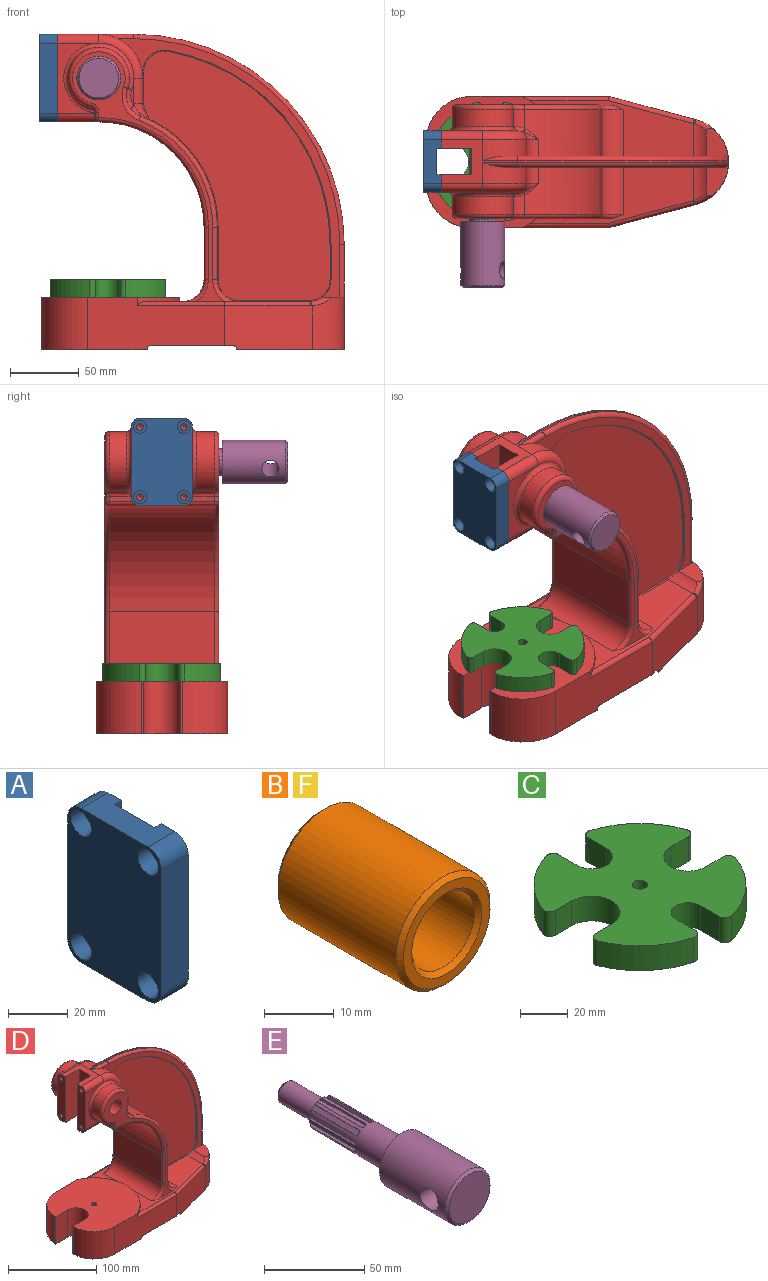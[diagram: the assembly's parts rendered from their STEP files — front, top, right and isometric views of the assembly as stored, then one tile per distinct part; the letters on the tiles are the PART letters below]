
ASSEMBLY  parts=6 mates=4
PART A: 26 faces, bbox 12.7x44.5x63.5 mm
  f0: plane 63.5x12.7mm, normal (1,0,0), area 753.5mm2, adj f1,f2,f6,f7,f8,f14,f17,f25
  f1: cylinder r=6.35mm len=12.7mm, axis (1,0,0), area 126.7mm2, adj f0,f2,f8,f9
  f2: plane 31.75x12.7mm, normal (0,0,1), area 341.8mm2, adj f0,f1,f3,f9,f10,f23,f24,f25
  f3: cylinder r=6.35mm len=12.7mm, axis (1,0,0), area 126.7mm2, adj f2,f4,f9,f10
  f4: plane 50.8x12.7mm, normal (0,1,0), area 645.2mm2, adj f3,f5,f9,f10
  f5: cylinder r=6.35mm len=12.7mm, axis (1,0,0), area 126.7mm2, adj f4,f6,f9,f10
  f6: plane 31.75x12.7mm, normal (0,0,-1), area 341.8mm2, adj f0,f5,f7,f9,f10,f23,f24,f25
  f7: cylinder r=6.35mm len=12.7mm, axis (1,0,0), area 126.7mm2, adj f0,f6,f8,f9
  f8: plane 50.8x12.7mm, normal (0,-1,0), area 645.2mm2, adj f0,f1,f7,f9
  f9: plane 63.5x44.45mm, normal (-1,0,0), area 2502.9mm2, adj f1,f2,f3,f4,f5,f6,f7,f8
  f10: plane 63.5x12.7mm, normal (1,0,0), area 753.5mm2, adj f2,f3,f4,f5,f6,f11,f20,f24
  f11: cylinder r=2.38mm len=6.35mm, axis (-1,0,0), area 95mm2, adj f10,f12
  f12: plane 9.53x9.53mm, normal (-1,0,0), area 53.4mm2, adj f11,f13
  f13: cylinder r=4.76mm len=9.53mm, axis (-1,0,0), area 190mm2, adj f9,f12
  f14: cylinder r=2.38mm len=6.35mm, axis (-1,0,0), area 95mm2, adj f0,f15
  f15: plane 9.53x9.53mm, normal (-1,0,0), area 53.4mm2, adj f14,f16
  f16: cylinder r=4.76mm len=9.53mm, axis (-1,0,0), area 190mm2, adj f9,f15
  f17: cylinder r=2.38mm len=6.35mm, axis (-1,0,0), area 95mm2, adj f0,f18
  f18: plane 9.53x9.53mm, normal (-1,0,0), area 53.4mm2, adj f17,f19
  f19: cylinder r=4.76mm len=9.53mm, axis (-1,0,0), area 190mm2, adj f9,f18
  f20: cylinder r=2.38mm len=6.35mm, axis (-1,0,0), area 95mm2, adj f10,f21
  f21: plane 9.53x9.53mm, normal (-1,0,0), area 53.4mm2, adj f20,f22
  f22: cylinder r=4.76mm len=9.53mm, axis (-1,0,0), area 190mm2, adj f9,f21
  f23: plane 63.5x19.05mm, normal (1,0,0), area 1209.7mm2, adj f2,f6,f24,f25
  f24: plane 63.5x3.23mm, normal (0,-1,0), area 204.8mm2, adj f2,f6,f10,f23
  f25: plane 63.5x3.23mm, normal (0,1,0), area 204.8mm2, adj f0,f2,f6,f23
PART B: 8 faces, bbox 19.1x25.4x19.1 mm
  f0: plane 17.53x17.53mm, normal (0,-1,0), area 82.3mm2, adj f4,f5
  f1: plane 17.53x17.53mm, normal (0,1,0), area 82.3mm2, adj f6,f7
  f2: cylinder r=9.53mm len=23.88mm, axis (0,1,0), area 1428.9mm2, adj f4,f7
  f3: cylinder r=6.35mm len=23.88mm, axis (0,1,0), area 952.6mm2, adj f5,f6
  f4: cone r=9.53mm half-angle=45deg, axis (0,1,0), area 61.9mm2, adj f0,f2
  f5: cone r=6.35mm half-angle=45deg, axis (0,-1,0), area 45.6mm2, adj f0,f3
  f6: cone r=6.35mm half-angle=45deg, axis (0,1,0), area 45.6mm2, adj f1,f3
  f7: cone r=9.53mm half-angle=45deg, axis (0,-1,0), area 61.9mm2, adj f1,f2
PART C: 27 faces, bbox 83.8x85.8x12.7 mm
  f0: cylinder r=44.45mm len=28.56mm, axis (0,0,-1), area 510.6mm2, adj f17,f18,f19,f25
  f1: plane 12.7x9.85mm, normal (0,-1,0), area 125.1mm2, adj f2,f17,f18,f25
  f2: cylinder r=11.9mm len=23.8mm, axis (0,0,-1), area 474.8mm2, adj f1,f3,f17,f18
  f3: plane 12.7x9.85mm, normal (0,1,0), area 125.1mm2, adj f2,f17,f18,f26
  f4: cylinder r=44.45mm len=30.27mm, axis (0,0,-1), area 533.1mm2, adj f17,f18,f20,f26
  f5: plane 12.7x11.39mm, normal (1,0,0), area 144.7mm2, adj f6,f17,f18,f20
  f6: cylinder r=7.14mm len=14.28mm, axis (0,0,-1), area 284.8mm2, adj f5,f7,f17,f18
  f7: plane 12.7x11.39mm, normal (-1,0,0), area 144.7mm2, adj f6,f17,f18,f21
  f8: cylinder r=44.45mm len=30.9mm, axis (0,0,-1), area 556.3mm2, adj f17,f18,f21,f22
  f9: plane 12.7x10.43mm, normal (0,1,0), area 132.5mm2, adj f10,f17,f18,f22
  f10: cylinder r=10.31mm len=20.62mm, axis (0,0,-1), area 411.4mm2, adj f9,f11,f17,f18
  f11: plane 12.7x10.43mm, normal (0,-1,0), area 132.5mm2, adj f10,f17,f18,f23
  f12: cylinder r=44.45mm len=29.19mm, axis (0,0,-1), area 533.7mm2, adj f17,f18,f23,f24
  f13: plane 12.7x10.95mm, normal (-1,0,0), area 139mm2, adj f14,f17,f18,f24
  f14: cylinder r=8.72mm len=17.45mm, axis (0,0,-1), area 348.1mm2, adj f13,f15,f17,f18
  f15: plane 12.7x10.95mm, normal (1,0,0), area 139mm2, adj f14,f17,f18,f19
  f16: cylinder r=3.17mm len=12.7mm, axis (0,0,-1), area 253.4mm2, adj f17,f18
  f17: plane 85.84x83.78mm, normal (0,0,1), area 4373.8mm2, adj f0,f1,f2,f3,f4,f5,f6,f7
  f18: plane 85.84x83.78mm, normal (0,0,-1), area 4373.8mm2, adj f0,f1,f2,f3,f4,f5,f6,f7
  f19: cylinder r=3.17mm len=12.7mm, axis (0,0,-1), area 75.1mm2, adj f0,f15,f17,f18
  f20: cylinder r=3.17mm len=12.7mm, axis (0,0,-1), area 73.5mm2, adj f4,f5,f17,f18
  f21: cylinder r=3.17mm len=12.7mm, axis (0,0,-1), area 73.5mm2, adj f7,f8,f17,f18
  f22: cylinder r=3.17mm len=12.7mm, axis (0,0,-1), area 76.8mm2, adj f8,f9,f17,f18
  f23: cylinder r=3.17mm len=12.7mm, axis (0,0,-1), area 76.8mm2, adj f11,f12,f17,f18
  f24: cylinder r=3.17mm len=12.7mm, axis (0,0,-1), area 75.1mm2, adj f12,f13,f17,f18
  f25: cylinder r=3.17mm len=12.7mm, axis (0,0,-1), area 78.4mm2, adj f0,f1,f17,f18
  f26: cylinder r=3.17mm len=12.7mm, axis (0,0,-1), area 78.4mm2, adj f3,f4,f17,f18
PART D: 180 faces, bbox 234.5x98.1x244 mm
  f0: plane 63.5x12.7mm, normal (-1,0,0), area 753.5mm2, adj f2,f15,f17,f92,f97,f149,f151,f158
  f1: plane 20.23x2.34mm, normal (0,1,0), area 23.9mm2, adj f90,f91,f104,f106
  f2: plane 50.8x30.1mm, normal (0,-1,0), area 515.4mm2, adj f0,f83,f92,f97,f124
  f3: plane 22.59x12.73mm, normal (1,0,0), area 235.4mm2, adj f19,f26,f32,f87,f94,f174
  f4: plane 22.59x12.73mm, normal (1,0,0), area 235.4mm2, adj f10,f14,f33,f86,f90,f164
  f5: plane 99.19x38.1mm, normal (0,-1,0), area 3202mm2, adj f6,f40,f46,f49,f52,f58,f76,f133
  f6: plane 100x95.25mm, normal (0,0,1), area 7398mm2, adj f5,f43,f44,f48,f54,f55,f56,f57
  f7: plane 38.1x34.96mm, normal (1,0,0), area 1331.9mm2, adj f8,f9,f114,f169
  f8: cylinder r=15.88mm len=34.96mm, axis (0,1,0), area 871.7mm2, adj f7,f37,f115,f167
  f9: cylinder r=85.72mm len=80.21mm, axis (0,1,0), area 3442.3mm2, adj f7,f80,f86,f100,f113,f168
  f10: cylinder r=15.88mm len=18.65mm, axis (0,1,0), area 22.7mm2, adj f4,f11,f33,f162
  f11: cylinder r=142.88mm len=140.67mm, axis (0,1,0), area 163.3mm2, adj f10,f12,f33,f160
  f12: plane 25.4x0.82mm, normal (-1,0,0), area 20.8mm2, adj f11,f13,f33,f161
  f13: cylinder r=15.88mm len=24.81mm, axis (0,1,0), area 242.1mm2, adj f12,f33,f37,f45,f139,f140,f163
  f14: cylinder r=31.75mm len=31.75mm, axis (0,1,0), area 616.8mm2, adj f4,f15,f33,f89,f141
  f15: plane 55.5x31.75mm, normal (0,0,1), area 573.2mm2, adj f0,f14,f16,f19,f31,f88,f92,f141
  f16: plane 63.5x12.7mm, normal (-1,0,0), area 753.5mm2, adj f15,f17,f21,f88,f96,f147,f153,f157
  f17: plane 31.75x30.1mm, normal (0,0,-1), area 533.2mm2, adj f0,f16,f18,f96,f97,f156,f157,f158
  f18: cylinder r=76.2mm len=76.2mm, axis (0,1,0), area 9120.7mm2, adj f17,f22,f103,f105,f119,f121
  f19: cylinder r=31.75mm len=31.75mm, axis (0,1,0), area 616.8mm2, adj f3,f15,f32,f93,f144
  f20: plane 20.23x2.34mm, normal (0,-1,0), area 23.9mm2, adj f94,f95,f122,f124
  f21: plane 50.8x30.1mm, normal (0,1,0), area 515.4mm2, adj f16,f78,f88,f96,f106
  f22: plane 76.2x38.1mm, normal (-1,0,0), area 2903.2mm2, adj f18,f98,f101,f117
  f23: cylinder r=15.88mm len=34.96mm, axis (0,1,0), area 871.7mm2, adj f24,f37,f132,f177
  f24: plane 38.1x34.96mm, normal (1,0,0), area 1331.9mm2, adj f23,f25,f131,f179
  f25: cylinder r=85.72mm len=80.21mm, axis (0,1,0), area 3442.3mm2, adj f24,f81,f87,f118,f130,f178
  f26: cylinder r=15.88mm len=18.65mm, axis (0,1,0), area 22.7mm2, adj f3,f27,f32,f172
  f27: cylinder r=142.88mm len=140.67mm, axis (0,1,0), area 163.3mm2, adj f26,f28,f32,f170
  f28: plane 25.4x0.82mm, normal (-1,0,0), area 20.8mm2, adj f27,f29,f32,f171
  f29: cylinder r=15.88mm len=24.81mm, axis (0,1,0), area 242.1mm2, adj f28,f32,f36,f37,f135,f136,f173
  f30: plane 76.2x7.92mm, normal (1,0,0), area 361.9mm2, adj f31,f36,f42,f45,f51,f53,f143,f146
  f31: cylinder r=152.4mm len=152.4mm, axis (0,1,0), area 377mm2, adj f15,f30,f142,f145
  f32: plane 187.33x160.79mm, normal (0,-1,0), area 1900.4mm2, adj f3,f19,f26,f27,f28,f29,f36,f144
  f33: plane 187.33x160.79mm, normal (0,1,0), area 1900.4mm2, adj f4,f10,f11,f12,f13,f14,f45,f141
  f34: plane 180.67x135mm, normal (0,-1,0), area 14138.8mm2, adj f170,f171,f172,f173,f174,f175,f176,f177
  f35: plane 180.67x135mm, normal (0,1,0), area 14138.8mm2, adj f160,f161,f162,f163,f164,f165,f166,f167
  f36: plane 26.58x18.73mm, normal (0,0,1), area 245.8mm2, adj f29,f30,f32,f53,f136,f146
  f37: plane 119.12x89.67mm, normal (0,0,1), area 4280.2mm2, adj f8,f13,f23,f29,f76,f77,f84,f98
  f38: cylinder r=3.17mm len=9.06mm, axis (0,1,0), area 40.9mm2, adj f40,f42,f52,f69
  f39: cylinder r=3.17mm len=7.93mm, axis (0,1,0), area 39.5mm2, adj f41,f46,f48,f65
  f40: plane 58.73x9.7mm, normal (0,0,-1), area 467.1mm2, adj f5,f38,f49,f52,f64,f69
  f41: plane 58.73x9.7mm, normal (0,0,-1), area 467.1mm2, adj f39,f47,f48,f50,f65,f67
  f42: plane 90.55x77.8mm, normal (0,0,-1), area 1454mm2, adj f30,f38,f47,f50,f51,f52,f53,f59
  f43: plane 38.1x1.61mm, normal (-1,0,0), area 61.5mm2, adj f6,f46,f54,f58
  f44: plane 38.1x1.61mm, normal (-1,0,0), area 61.5mm2, adj f6,f46,f55,f57
  f45: plane 26.58x18.73mm, normal (0,0,1), area 245.8mm2, adj f13,f30,f33,f51,f140,f143
  f46: plane 95.25x76.2mm, normal (0,0,-1), area 2029.8mm2, adj f5,f39,f43,f44,f48,f49,f54,f55
  f47: cylinder r=3.17mm len=9.06mm, axis (0,1,0), area 40.9mm2, adj f41,f42,f50,f67
  f48: plane 99.19x38.1mm, normal (0,1,0), area 3202mm2, adj f6,f39,f41,f46,f50,f57,f76,f137
  f49: cylinder r=3.17mm len=7.93mm, axis (0,1,0), area 39.5mm2, adj f5,f40,f46,f64
  f50: plane 63.64x32.15mm, normal (0.26,0.97,0), area 2053.6mm2, adj f41,f42,f47,f48,f51,f138,f139
  f51: cylinder r=31.75mm len=38.1mm, axis (0,0,-1), area 1379.2mm2, adj f30,f42,f45,f50,f140
  f52: plane 63.64x32.15mm, normal (0.26,-0.97,0), area 2053.6mm2, adj f5,f38,f40,f42,f53,f134,f135
  f53: cylinder r=31.75mm len=38.1mm, axis (0,0,-1), area 1379.2mm2, adj f30,f36,f42,f52,f136
  f54: plane 38.1x19.05mm, normal (0,1,0), area 725.8mm2, adj f6,f43,f46,f56
  f55: plane 38.1x19.05mm, normal (0,-1,0), area 725.8mm2, adj f6,f44,f46,f56
  f56: cylinder r=13.49mm len=38.1mm, axis (0,0,-1), area 1615.1mm2, adj f6,f46,f54,f55
  f57: cylinder r=33.32mm len=38.1mm, axis (0,0,-1), area 1963.7mm2, adj f6,f44,f46,f48
  f58: cylinder r=33.32mm len=38.1mm, axis (0,0,-1), area 1963.7mm2, adj f5,f6,f43,f46
  f59: plane 30.18x6.86mm, normal (-1,0,0), area 207mm2, adj f42,f60,f68,f70
  f60: plane 31.27x5.6mm, normal (0,0,-1), area 124.1mm2, adj f59,f61,f68,f70
  f61: cylinder r=23.8mm len=46.06mm, axis (0,1,0), area 499.2mm2, adj f60,f62,f67,f68,f69,f70
  f62: plane 84.13x79.4mm, normal (0,0,-1), area 5642.5mm2, adj f61,f64,f65,f66,f67,f69
  f63: plane 100.62x79.4mm, normal (0,0,-1), area 6568.5mm2, adj f64,f65,f66,f71,f72,f73,f74,f75
  f64: plane 98.15x30.18mm, normal (0,1,0), area 2718.8mm2, adj f40,f46,f49,f62,f63,f66,f69,f75
  f65: plane 98.15x30.18mm, normal (0,-1,0), area 2718.8mm2, adj f39,f41,f46,f62,f63,f66,f67,f74
  f66: plane 79.4x3.18mm, normal (-1,0,0), area 252.1mm2, adj f62,f63,f64,f65
  f67: plane 62.63x27.36mm, normal (-0.26,-0.97,0), area 1710.8mm2, adj f41,f42,f47,f61,f62,f65,f68
  f68: cylinder r=23.83mm len=30.18mm, axis (0,0,-1), area 814.8mm2, adj f42,f59,f60,f61,f67
  f69: plane 62.63x27.36mm, normal (-0.26,0.97,0), area 1710.8mm2, adj f38,f40,f42,f61,f62,f64,f70
  f70: cylinder r=23.83mm len=30.18mm, axis (0,0,-1), area 814.8mm2, adj f42,f59,f60,f61,f69
  f71: plane 30.18x10.12mm, normal (0,-1,0), area 305.3mm2, adj f46,f63,f73,f75
  f72: plane 30.18x10.12mm, normal (0,1,0), area 305.3mm2, adj f46,f63,f73,f74
  f73: cylinder r=21.42mm len=42.84mm, axis (0,0,-1), area 2030.4mm2, adj f46,f63,f71,f72
  f74: cylinder r=25.4mm len=30.18mm, axis (0,0,-1), area 986.2mm2, adj f46,f63,f65,f72
  f75: cylinder r=25.4mm len=30.18mm, axis (0,0,-1), area 986.2mm2, adj f46,f63,f64,f71
  f76: cylinder r=52.37mm len=95.25mm, axis (0,0,1), area 401mm2, adj f5,f6,f37,f48,f133,f137
  f77: plane 180.98x110.12mm, normal (0,1,0), area 1717.8mm2, adj f37,f85,f99,f101,f103,f109,f110,f111
  f78: plane 16.73x3.98mm, normal (-1,0,0), area 64.1mm2, adj f21,f96,f105,f106,f108,f109
  f79: cylinder r=22.23mm len=44.45mm, axis (0,1,0), area 1356.2mm2, adj f80,f106,f108,f111
  f80: cylinder r=15.88mm len=20.22mm, axis (0,1,0), area 319.4mm2, adj f9,f79,f102,f104,f112
  f81: cylinder r=15.88mm len=20.22mm, axis (0,1,0), area 319.4mm2, adj f25,f82,f120,f122,f129
  f82: cylinder r=22.23mm len=44.45mm, axis (0,1,0), area 1356.2mm2, adj f81,f124,f126,f128
  f83: plane 16.73x3.98mm, normal (-1,0,0), area 64.1mm2, adj f2,f97,f121,f124,f125,f126
  f84: plane 180.98x110.12mm, normal (0,-1,0), area 1717.8mm2, adj f37,f85,f116,f117,f119,f125,f127,f128
  f85: cylinder r=9.53mm len=82.55mm, axis (0,1,0), area 4727mm2, adj f77,f84,f156,f157,f158,f159
  f86: cylinder r=15.88mm len=14.02mm, axis (0,1,0), area 218.9mm2, adj f4,f9,f91,f166
  f87: cylinder r=15.88mm len=14.02mm, axis (0,1,0), area 218.9mm2, adj f3,f25,f95,f176
  f88: cylinder r=6.35mm len=30.1mm, axis (-1,0,0), area 300.2mm2, adj f15,f16,f21,f89
  f89: torus R=25.4mm, axis (0,-1,0), area 461.3mm2, adj f14,f88,f90,f106
  f90: cylinder r=6.35mm len=18.2mm, axis (0,0,1), area 181.6mm2, adj f1,f4,f89,f91
  f91: torus R=22.23mm, axis (0,-1,0), area 98mm2, adj f1,f86,f90,f100,f102
  f92: cylinder r=6.35mm len=30.1mm, axis (1,0,0), area 300.2mm2, adj f0,f2,f15,f93
  f93: torus R=25.4mm, axis (0,-1,0), area 461.3mm2, adj f19,f92,f94,f124
  f94: cylinder r=6.35mm len=18.2mm, axis (0,0,-1), area 181.6mm2, adj f3,f20,f93,f95
  f95: torus R=22.23mm, axis (0,-1,0), area 98mm2, adj f20,f87,f94,f118,f120
  f96: cylinder r=6.35mm len=30.1mm, axis (1,0,0), area 279.1mm2, adj f16,f17,f21,f78,f105
  f97: cylinder r=6.35mm len=30.1mm, axis (-1,0,0), area 279.1mm2, adj f0,f2,f17,f83,f121
  f98: cylinder r=15.88mm len=76.2mm, axis (0,-1,0), area 1900.2mm2, adj f22,f37,f99,f116
  f99: torus R=19.05mm, axis (0,-1,0), area 107.7mm2, adj f37,f77,f98,f101
  f100: bspline ~12.01x8.85mm, area 17.9mm2, adj f9,f91,f102
  f101: cylinder r=3.17mm len=38.1mm, axis (0,0,-1), area 190mm2, adj f22,f77,f99,f103
  f102: bspline ~10.6x9.56mm, area 36.6mm2, adj f80,f91,f100,f104
  f103: torus R=79.38mm, axis (0,-1,0), area 606mm2, adj f18,f77,f101,f107
  f104: torus R=12.7mm, axis (0,-1,0), area 70.6mm2, adj f1,f80,f102,f106
  f105: cylinder r=3.17mm len=22.23mm, axis (0,1,0), area 97.1mm2, adj f18,f78,f96,f107
  f106: torus R=25.4mm, axis (0,-1,0), area 570mm2, adj f1,f21,f78,f79,f89,f104,f108
  f107: sphere r=3.17mm, area 21.6mm2, adj f103,f105,f109
  f108: cylinder r=3.17mm len=15.82mm, axis (0,1,0), area 59.7mm2, adj f78,f79,f106,f110
  f109: cylinder r=3.17mm len=3.98mm, axis (0,0,-1), area 19.9mm2, adj f77,f78,f107,f110
  f110: torus R=6.35mm, axis (0,-1,0), area 28.5mm2, adj f77,f108,f109,f111
  f111: torus R=19.05mm, axis (0,-1,0), area 504.9mm2, adj f77,f79,f110,f112
  f112: torus R=19.05mm, axis (0,-1,0), area 132.1mm2, adj f77,f80,f111,f113
  f113: torus R=82.55mm, axis (0,-1,0), area 510.4mm2, adj f9,f77,f112,f114
  f114: cylinder r=3.17mm len=38.1mm, axis (0,0,1), area 190mm2, adj f7,f77,f113,f115
  f115: torus R=19.05mm, axis (0,-1,0), area 107.7mm2, adj f8,f37,f77,f114
  f116: torus R=19.05mm, axis (0,-1,0), area 107.7mm2, adj f37,f84,f98,f117
  f117: cylinder r=3.17mm len=38.1mm, axis (0,0,1), area 190mm2, adj f22,f84,f116,f119
  f118: bspline ~11.06x8.44mm, area 17.9mm2, adj f25,f95,f120
  f119: torus R=79.38mm, axis (0,-1,0), area 606mm2, adj f18,f84,f117,f123
  f120: bspline ~9.12x8.99mm, area 36.6mm2, adj f81,f95,f118,f122
  f121: cylinder r=3.17mm len=22.23mm, axis (0,1,0), area 97.1mm2, adj f18,f83,f97,f123
  f122: torus R=12.7mm, axis (0,-1,0), area 70.6mm2, adj f20,f81,f120,f124
  f123: sphere r=3.17mm, area 15.8mm2, adj f119,f121,f125
  f124: torus R=25.4mm, axis (0,-1,0), area 570mm2, adj f2,f20,f82,f83,f93,f122,f126
  f125: cylinder r=3.17mm len=3.98mm, axis (0,0,1), area 19.9mm2, adj f83,f84,f123,f127
  f126: cylinder r=3.17mm len=15.82mm, axis (0,1,0), area 59.7mm2, adj f82,f83,f124,f127
  f127: torus R=6.35mm, axis (0,-1,0), area 28.5mm2, adj f84,f125,f126,f128
  f128: torus R=19.05mm, axis (0,-1,0), area 504.9mm2, adj f82,f84,f127,f129
  f129: torus R=19.05mm, axis (0,-1,0), area 132.1mm2, adj f81,f84,f128,f130
  f130: torus R=82.55mm, axis (0,-1,0), area 510.4mm2, adj f25,f84,f129,f131
  f131: cylinder r=3.17mm len=38.1mm, axis (0,0,-1), area 190mm2, adj f24,f84,f130,f132
  f132: torus R=19.05mm, axis (0,-1,0), area 107.7mm2, adj f23,f37,f84,f131
  f133: cylinder r=3.17mm len=63.09mm, axis (1,0,0), area 298.9mm2, adj f5,f37,f76,f134
  f134: cylinder r=3.17mm len=62.81mm, axis (0.97,0.26,0), area 319mm2, adj f37,f52,f133,f135
  f135: bspline ~3.41x3.21mm, area 6mm2, adj f29,f52,f134,f136
  f136: bspline ~18.95x11.92mm, area 79.7mm2, adj f29,f36,f53,f135
  f137: cylinder r=3.17mm len=63.09mm, axis (-1,0,0), area 298.9mm2, adj f37,f48,f76,f138
  f138: cylinder r=3.17mm len=62.81mm, axis (-0.97,0.26,0), area 319mm2, adj f37,f50,f137,f139
  f139: bspline ~6.89x4.84mm, area 6mm2, adj f13,f50,f138,f140
  f140: bspline ~17.46x11.57mm, area 79.7mm2, adj f13,f45,f51,f139
  f141: cylinder r=3.17mm len=25.4mm, axis (-1,0,0), area 92.2mm2, adj f14,f15,f33,f142
  f142: torus R=149.22mm, axis (0,-1,0), area 1184.9mm2, adj f31,f33,f141,f143
  f143: cylinder r=3.17mm len=38.1mm, axis (0,0,1), area 190mm2, adj f30,f33,f45,f142
  f144: cylinder r=3.17mm len=25.4mm, axis (1,0,0), area 92.2mm2, adj f15,f19,f32,f145
  f145: torus R=149.22mm, axis (0,-1,0), area 1184.9mm2, adj f31,f32,f144,f146
  f146: cylinder r=3.17mm len=38.1mm, axis (0,0,-1), area 190mm2, adj f30,f32,f36,f145
  f147: cylinder r=2.38mm len=6.35mm, axis (-1,0,0), area 95mm2, adj f16,f148
  f148: cone r=0mm half-angle=59deg, axis (-1,0,0), area 20.8mm2, adj f147
  f149: cylinder r=2.38mm len=6.35mm, axis (-1,0,0), area 95mm2, adj f0,f150
  f150: cone r=0mm half-angle=59deg, axis (-1,0,0), area 20.8mm2, adj f149
  f151: cylinder r=2.38mm len=6.35mm, axis (-1,0,0), area 95mm2, adj f0,f152
  f152: cone r=0mm half-angle=59deg, axis (-1,0,0), area 20.8mm2, adj f151
  f153: cylinder r=2.38mm len=6.35mm, axis (-1,0,0), area 95mm2, adj f16,f154
  f154: cone r=0mm half-angle=59deg, axis (-1,0,0), area 20.8mm2, adj f153
  f155: cylinder r=3.17mm len=7.93mm, axis (0,0,1), area 158.1mm2, adj f6,f63
  f156: plane 26.47x19.05mm, normal (-1,0,0), area 504.2mm2, adj f17,f85,f157,f158
  f157: plane 63.5x22.17mm, normal (0,-1,0), area 1396.6mm2, adj f15,f16,f17,f85,f156,f159
  f158: plane 63.5x22.17mm, normal (0,1,0), area 1396.6mm2, adj f0,f15,f17,f85,f156,f159
  f159: plane 26.47x19.05mm, normal (-1,0,0), area 504.2mm2, adj f15,f85,f157,f158
  f160: torus R=142.11mm, axis (0,-1,0), area 238.1mm2, adj f11,f35,f161,f162
  f161: cylinder r=0.76mm len=25.4mm, axis (0,0,1), area 30.4mm2, adj f12,f35,f160,f163
  f162: torus R=15.11mm, axis (0,-1,0), area 32.6mm2, adj f10,f35,f160,f164
  f163: torus R=15.11mm, axis (0,-1,0), area 29.3mm2, adj f13,f35,f161,f165
  f164: cylinder r=0.76mm len=22.59mm, axis (0,0,1), area 27mm2, adj f4,f35,f162,f166
  f165: cylinder r=0.76mm len=50.8mm, axis (1,0,0), area 60.8mm2, adj f35,f37,f163,f167
  f166: torus R=15.11mm, axis (0,-1,0), area 20.2mm2, adj f35,f86,f164,f168
  f167: torus R=15.11mm, axis (0,-1,0), area 29.3mm2, adj f8,f35,f165,f169
  f168: torus R=86.49mm, axis (0,-1,0), area 111.5mm2, adj f9,f35,f166,f169
  f169: cylinder r=0.76mm len=38.1mm, axis (0,0,-1), area 45.6mm2, adj f7,f35,f167,f168
  f170: torus R=142.11mm, axis (0,-1,0), area 238.1mm2, adj f27,f34,f171,f172
  f171: cylinder r=0.76mm len=25.4mm, axis (0,0,-1), area 30.4mm2, adj f28,f34,f170,f173
  f172: torus R=15.11mm, axis (0,-1,0), area 32.6mm2, adj f26,f34,f170,f174
  f173: torus R=15.11mm, axis (0,-1,0), area 29.3mm2, adj f29,f34,f171,f175
  f174: cylinder r=0.76mm len=22.59mm, axis (0,0,-1), area 27mm2, adj f3,f34,f172,f176
  f175: cylinder r=0.76mm len=50.8mm, axis (-1,0,0), area 60.8mm2, adj f34,f37,f173,f177
  f176: torus R=15.11mm, axis (0,-1,0), area 20.2mm2, adj f34,f87,f174,f178
  f177: torus R=15.11mm, axis (0,-1,0), area 29.3mm2, adj f23,f34,f175,f179
  f178: torus R=86.49mm, axis (0,-1,0), area 111.5mm2, adj f25,f34,f176,f179
  f179: cylinder r=0.76mm len=38.1mm, axis (0,0,1), area 45.6mm2, adj f24,f34,f177,f178
PART E: 94 faces, bbox 31.8x130.2x31.8 mm
  f0: cone r=8mm half-angle=45deg, axis (0,-1,0), area 3.4mm2, adj f11,f18,f83,f87
  f1: cone r=8mm half-angle=45deg, axis (0,-1,0), area 3.4mm2, adj f11,f18,f77,f81
  f2: cone r=8mm half-angle=45deg, axis (0,-1,0), area 3.4mm2, adj f11,f18,f71,f75
  f3: cone r=8mm half-angle=45deg, axis (0,-1,0), area 3.4mm2, adj f11,f18,f65,f69
  f4: cone r=8mm half-angle=45deg, axis (0,-1,0), area 3.4mm2, adj f11,f18,f59,f63
  f5: cone r=8mm half-angle=45deg, axis (0,-1,0), area 3.4mm2, adj f11,f18,f53,f57
  f6: cone r=8mm half-angle=45deg, axis (0,-1,0), area 3.4mm2, adj f11,f18,f47,f51
  f7: cone r=8mm half-angle=45deg, axis (0,-1,0), area 3.4mm2, adj f11,f18,f41,f45
  f8: cone r=8mm half-angle=45deg, axis (0,-1,0), area 3.4mm2, adj f11,f18,f35,f39
  f9: cone r=8mm half-angle=45deg, axis (0,-1,0), area 3.4mm2, adj f11,f18,f29,f33
  f10: cone r=8mm half-angle=45deg, axis (0,-1,0), area 3.4mm2, adj f11,f18,f23,f27
  f11: cylinder r=9.53mm len=55.63mm, axis (0,-1,0), area 2118.8mm2, adj f0,f1,f2,f3,f4,f5,f6,f7
  f12: plane 31.75x31.75mm, normal (0,1,0), area 506.7mm2, adj f11,f13
  f13: cylinder r=15.88mm len=46.1mm, axis (0,-1,0), area 4339.6mm2, adj f12,f15,f16
  f14: plane 28.7x28.7mm, normal (0,-1,0), area 647mm2, adj f15
  f15: cone r=14.35mm half-angle=45deg, axis (0,1,0), area 204.7mm2, adj f13,f14
  f16: cylinder r=6.35mm len=31.75mm, axis (1,0,0), area 1214.5mm2, adj f13
  f17: cylinder r=6.35mm len=23.88mm, axis (0,1,0), area 952.6mm2, adj f18,f93
  f18: plane 16x16mm, normal (0,1,0), area 67.3mm2, adj f0,f1,f2,f3,f4,f5,f6,f7
  f19: plane 9.65x9.65mm, normal (0,1,0), area 73.2mm2, adj f93
  f20: cone r=8mm half-angle=45deg, axis (0,-1,0), area 3.4mm2, adj f11,f18,f21,f89
  f21: plane 31.76x1.55mm, normal (0.36,0,-0.93), area 51.4mm2, adj f11,f18,f20,f22,f24
  f22: plane 31.75x2.7mm, normal (0.97,0,0.26), area 88.7mm2, adj f18,f21,f23,f25
  f23: plane 31.76x1.65mm, normal (-0.15,0,0.99), area 51.4mm2, adj f10,f11,f18,f22,f26
  f24: cone r=1.78mm half-angle=83.9deg, axis (0.26,0,-0.97), area 1.5mm2, adj f11,f21,f25
  f25: cylinder r=1.78mm len=3.16mm, axis (0.26,0,-0.97), area 7.7mm2, adj f11,f22,f24,f26
  f26: cone r=0mm half-angle=83.9deg, axis (-0.26,0,0.97), area 1.5mm2, adj f11,f23,f25
  f27: plane 31.76x1.65mm, normal (-0.15,0,-0.99), area 51.4mm2, adj f10,f11,f18,f28,f30
  f28: plane 31.75x2.7mm, normal (0.97,0,-0.26), area 88.7mm2, adj f18,f27,f29,f31
  f29: plane 31.76x1.55mm, normal (0.36,0,0.93), area 51.4mm2, adj f9,f11,f18,f28,f32
  f30: cone r=1.78mm half-angle=83.9deg, axis (-0.26,0,-0.97), area 1.5mm2, adj f11,f27,f31
  f31: cylinder r=1.78mm len=3.16mm, axis (-0.26,0,-0.97), area 7.7mm2, adj f11,f28,f30,f32
  f32: cone r=0mm half-angle=83.9deg, axis (0.26,0,0.97), area 1.5mm2, adj f11,f29,f31
  f33: plane 31.76x1.3mm, normal (-0.63,0,-0.78), area 51.4mm2, adj f9,f11,f18,f34,f36
  f34: plane 31.75x1.98mm, normal (0.71,0,-0.71), area 88.7mm2, adj f18,f33,f35,f37
  f35: plane 31.76x1.3mm, normal (0.78,0,0.63), area 51.4mm2, adj f8,f11,f18,f34,f38
  f36: cone r=1.78mm half-angle=83.9deg, axis (-0.71,0,-0.71), area 1.5mm2, adj f11,f33,f37
  f37: cylinder r=1.78mm len=3.16mm, axis (-0.71,0,-0.71), area 7.5mm2, adj f11,f34,f36,f38
  f38: cone r=0mm half-angle=83.9deg, axis (0.71,0,0.71), area 1.5mm2, adj f11,f35,f37
  f39: plane 31.76x1.55mm, normal (-0.93,0,-0.36), area 51.4mm2, adj f8,f11,f18,f40,f42
  f40: plane 31.75x2.7mm, normal (0.26,0,-0.97), area 88.7mm2, adj f18,f39,f41,f43
  f41: plane 31.76x1.65mm, normal (0.99,0,0.15), area 51.4mm2, adj f7,f11,f18,f40,f44
  f42: cone r=1.78mm half-angle=83.9deg, axis (-0.97,0,-0.26), area 1.5mm2, adj f11,f39,f43
  f43: cylinder r=1.78mm len=3.16mm, axis (-0.97,0,-0.26), area 7.7mm2, adj f11,f40,f42,f44
  f44: cone r=0mm half-angle=83.9deg, axis (0.97,0,0.26), area 1.5mm2, adj f11,f41,f43
  f45: plane 31.76x1.65mm, normal (-0.99,0,0.15), area 51.4mm2, adj f7,f11,f18,f46,f48
  f46: plane 31.75x2.7mm, normal (-0.26,0,-0.97), area 88.7mm2, adj f18,f45,f47,f49
  f47: plane 31.76x1.55mm, normal (0.93,0,-0.36), area 51.4mm2, adj f6,f11,f18,f46,f50
  f48: cone r=1.78mm half-angle=83.9deg, axis (-0.97,0,0.26), area 1.5mm2, adj f11,f45,f49
  f49: cylinder r=1.78mm len=3.16mm, axis (-0.97,0,0.26), area 7.7mm2, adj f11,f46,f48,f50
  f50: cone r=0mm half-angle=83.9deg, axis (0.97,0,-0.26), area 1.5mm2, adj f11,f47,f49
  f51: plane 31.76x1.3mm, normal (-0.78,0,0.63), area 51.4mm2, adj f6,f11,f18,f52,f54
  f52: plane 31.75x1.98mm, normal (-0.71,0,-0.71), area 88.7mm2, adj f18,f51,f53,f55
  f53: plane 31.76x1.3mm, normal (0.63,0,-0.78), area 51.4mm2, adj f5,f11,f18,f52,f56
  f54: cone r=1.78mm half-angle=83.9deg, axis (-0.71,0,0.71), area 1.5mm2, adj f11,f51,f55
  f55: cylinder r=1.78mm len=3.16mm, axis (-0.71,0,0.71), area 7.5mm2, adj f11,f52,f54,f56
  f56: cone r=0mm half-angle=83.9deg, axis (0.71,0,-0.71), area 1.5mm2, adj f11,f53,f55
  f57: plane 31.76x1.55mm, normal (-0.36,0,0.93), area 51.4mm2, adj f5,f11,f18,f58,f60
  f58: plane 31.75x2.7mm, normal (-0.97,0,-0.26), area 88.7mm2, adj f18,f57,f59,f61
  f59: plane 31.76x1.65mm, normal (0.15,0,-0.99), area 51.4mm2, adj f4,f11,f18,f58,f62
  f60: cone r=1.78mm half-angle=83.9deg, axis (-0.26,0,0.97), area 1.5mm2, adj f11,f57,f61
  f61: cylinder r=1.78mm len=3.16mm, axis (-0.26,0,0.97), area 7.7mm2, adj f11,f58,f60,f62
  f62: cone r=0mm half-angle=83.9deg, axis (0.26,0,-0.97), area 1.5mm2, adj f11,f59,f61
  f63: plane 31.76x1.65mm, normal (0.15,0,0.99), area 51.4mm2, adj f4,f11,f18,f64,f66
  f64: plane 31.75x2.7mm, normal (-0.97,0,0.26), area 88.7mm2, adj f18,f63,f65,f67
  f65: plane 31.76x1.55mm, normal (-0.36,0,-0.93), area 51.4mm2, adj f3,f11,f18,f64,f68
  f66: cone r=1.78mm half-angle=83.9deg, axis (0.26,0,0.97), area 1.5mm2, adj f11,f63,f67
  f67: cylinder r=1.78mm len=3.16mm, axis (0.26,0,0.97), area 7.7mm2, adj f11,f64,f66,f68
  f68: cone r=0mm half-angle=83.9deg, axis (-0.26,0,-0.97), area 1.5mm2, adj f11,f65,f67
  f69: plane 31.76x1.3mm, normal (0.63,0,0.78), area 51.4mm2, adj f3,f11,f18,f70,f72
  f70: plane 31.75x1.98mm, normal (-0.71,0,0.71), area 88.7mm2, adj f18,f69,f71,f73
  f71: plane 31.76x1.3mm, normal (-0.78,0,-0.63), area 51.4mm2, adj f2,f11,f18,f70,f74
  f72: cone r=1.78mm half-angle=83.9deg, axis (0.71,0,0.71), area 1.5mm2, adj f11,f69,f73
  f73: cylinder r=1.78mm len=3.16mm, axis (0.71,0,0.71), area 7.5mm2, adj f11,f70,f72,f74
  f74: cone r=0mm half-angle=83.9deg, axis (-0.71,0,-0.71), area 1.5mm2, adj f11,f71,f73
  f75: plane 31.76x1.55mm, normal (0.93,0,0.36), area 51.4mm2, adj f2,f11,f18,f76,f78
  f76: plane 31.75x2.7mm, normal (-0.26,0,0.97), area 88.7mm2, adj f18,f75,f77,f79
  f77: plane 31.76x1.65mm, normal (-0.99,0,-0.15), area 51.4mm2, adj f1,f11,f18,f76,f80
  f78: cone r=1.78mm half-angle=83.9deg, axis (0.97,0,0.26), area 1.5mm2, adj f11,f75,f79
  f79: cylinder r=1.78mm len=3.16mm, axis (0.97,0,0.26), area 7.7mm2, adj f11,f76,f78,f80
  f80: cone r=0mm half-angle=83.9deg, axis (-0.97,0,-0.26), area 1.5mm2, adj f11,f77,f79
  f81: plane 31.76x1.65mm, normal (0.99,0,-0.15), area 51.4mm2, adj f1,f11,f18,f82,f84
  f82: plane 31.75x2.7mm, normal (0.26,0,0.97), area 88.7mm2, adj f18,f81,f83,f85
  f83: plane 31.76x1.55mm, normal (-0.93,0,0.36), area 51.4mm2, adj f0,f11,f18,f82,f86
  f84: cone r=1.78mm half-angle=83.9deg, axis (0.97,0,-0.26), area 1.5mm2, adj f11,f81,f85
  f85: cylinder r=1.78mm len=3.16mm, axis (0.97,0,-0.26), area 7.7mm2, adj f11,f82,f84,f86
  f86: cone r=0mm half-angle=83.9deg, axis (-0.97,0,0.26), area 1.5mm2, adj f11,f83,f85
  f87: plane 31.76x1.3mm, normal (0.78,0,-0.63), area 51.4mm2, adj f0,f11,f18,f88,f90
  f88: plane 31.75x1.98mm, normal (0.71,0,0.71), area 88.7mm2, adj f18,f87,f89,f91
  f89: plane 31.76x1.3mm, normal (-0.63,0,0.78), area 51.4mm2, adj f11,f18,f20,f88,f92
  f90: cone r=1.78mm half-angle=83.9deg, axis (0.71,0,-0.71), area 1.5mm2, adj f11,f87,f91
  f91: cylinder r=1.78mm len=3.16mm, axis (0.71,0,-0.71), area 7.5mm2, adj f11,f88,f90,f92
  f92: cone r=0mm half-angle=83.9deg, axis (-0.71,0,0.71), area 1.5mm2, adj f11,f89,f91
  f93: cone r=4.83mm half-angle=45deg, axis (0,-1,0), area 75.7mm2, adj f17,f19
PART F: same geometry as B
PLACE A t=(34.01,-3.36,8.37)mm
PLACE B t=(34.01,-61.27,8.37)mm
PLACE C rot(axis=(1,0,0),180deg) t=(34.01,-3.36,-296.43)mm
PLACE D t=(34.01,-3.36,8.37)mm fixed
PLACE E rot(axis=(0,-1,0),18.5deg) t=(34.01,-5.77,8.37)mm
PLACE F t=(34.01,-3.36,8.37)mm
MATE fastened A.f11 <-> D.f147  axis (1,0,0) through (3.91,12.51,33.77)mm
MATE revolute E.f0 <-> D.f14  axis (0,-1,0) through (34.01,-19.24,8.37)mm
MATE fastened B.f2 <-> D.f14  axis (0,1,0) through (34.01,-44.64,8.37)mm
MATE fastened C.f16 <-> D.f76  axis (0,0,-1) through (40.36,-3.36,-150.38)mm
